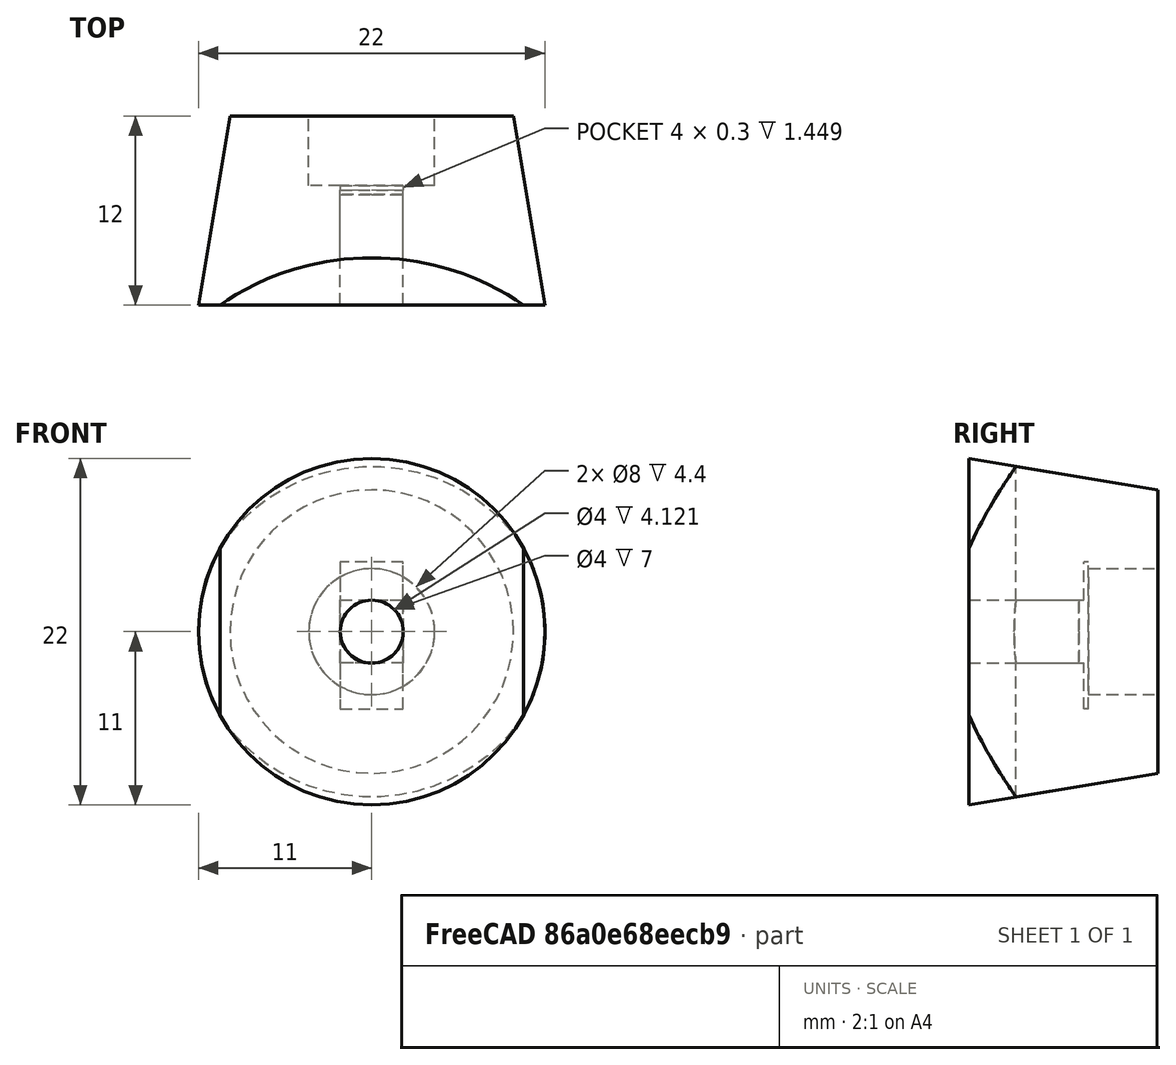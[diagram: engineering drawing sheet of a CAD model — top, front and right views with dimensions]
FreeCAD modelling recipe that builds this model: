
FCSTD DOCUMENT  (FreeCAD 0.19R)
Label: TrikeBumpers
License: All rights reserved
LicenseURL: http://en.wikipedia.org/wiki/All_rights_reserved
objects: Sketcher::SketchObject×4, PartDesign::Pocket×2, PartDesign::Revolution×1, Part::Cylinder×1, PartDesign::Pad×1, PartDesign::Body×1, Part::Cut×1, Mesh::Feature×1
note: 15 computed .brp shape members not serialized (recipe doc carries the construction recipe); baked Part::Feature solids carry a one-line shape summary decoded from their .brp

FEATURE [Sketcher::SketchObject] Sketch
  FullyConstrained = true
  MapMode = 5
  Support = -> [XY_Plane]
  sketch-geometry (6):
    g0: LineSegment StartX=2 StartY=7 StartZ=0 EndX=4 EndY=7 EndZ=0
    g1: LineSegment StartX=4 StartY=7 StartZ=0 EndX=4 EndY=12 EndZ=0
    g2: LineSegment StartX=4 StartY=12 StartZ=0 EndX=9 EndY=12 EndZ=0
    g3: LineSegment StartX=9 StartY=12 StartZ=0 EndX=11 EndY=0 EndZ=0
    g4: LineSegment StartX=11 StartY=0 StartZ=0 EndX=2 EndY=0 EndZ=0
    g5: LineSegment StartX=2 StartY=0 StartZ=0 EndX=2 EndY=7 EndZ=0
  constraints (18):
    c: Horizontal(g0)
    c: Coincident(g0,g1)
    c: Vertical(g1)
    c: Coincident(g1,g2)
    c: Horizontal(g2)
    c: Coincident(g2,g3)
    c: PointOnObject(g3,g-1)
    c: Coincident(g3,g4)
    c: PointOnObject(g4,g-1)
    c: Coincident(g4,g5)
    c: Coincident(g5,g0)
    c: Vertical(g5)
    c: DistanceX(g3) = 11
    c: DistanceX(g2) = 9
    c: DistanceX(g0) = 2
    c: DistanceX(g1) = 4
    c: Distance(g1) = 5
    c: DistanceY(g1) = 12
FEATURE [PartDesign::Revolution] Revolution
  Angle = 360
  Axis = (0,1,0)
  Base = (0,0,0)
  Profile = -> Sketch
  ReferenceAxis = -> Sketch [V_Axis]
  Reversed = true
FEATURE [Part::Cylinder] Cylinder
  Angle = 360
  AttacherType = Attacher::AttachEngine3D
  Height = 100
  Placement = pos=(0,-14,-20) rot=(0,0,1;0rad)
  Radius = 17
FEATURE [Sketcher::SketchObject] Sketch001
  FullyConstrained = false
  MapMode = 5
  Placement = pos=(0,7,0) rot=(0,0.707107,0.707107;3.14159rad)
  Support = -> [Revolution]
  sketch-geometry (4):
    g0: LineSegment StartX=-4.35972 StartY=4.85502 StartZ=0 EndX=4.65727 EndY=4.85502 EndZ=0
    g1: LineSegment StartX=4.65727 StartY=4.85502 StartZ=0 EndX=4.65727 EndY=-5.02854 EndZ=0
    g2: LineSegment StartX=4.65727 StartY=-5.02854 StartZ=0 EndX=-4.35972 EndY=-5.02854 EndZ=0
    g3: LineSegment StartX=-4.35972 StartY=-5.02854 StartZ=0 EndX=-4.35972 EndY=4.85502 EndZ=0
  constraints (8):
    c: Coincident(g0,g1)
    c: Coincident(g1,g2)
    c: Coincident(g2,g3)
    c: Coincident(g3,g0)
    c: Horizontal(g0)
    c: Horizontal(g2)
    c: Vertical(g1)
    c: Vertical(g3)
FEATURE [PartDesign::Pad] Pad
  BaseFeature = -> Revolution
  Direction = (1,1,1)
  Length = 0.6
  Length2 = 100
  Profile = -> Sketch001
  Type = 0
FEATURE [Sketcher::SketchObject] Sketch002
  FullyConstrained = false
  MapMode = 5
  Placement = pos=(0,7.6,-1.4e-15) rot=(0,0.707107,0.707107;3.14159rad)
  Support = -> [Pad]
  sketch-geometry (4):
    g0: LineSegment StartX=-2 StartY=4.41259 StartZ=0 EndX=2 EndY=4.41259 EndZ=0
    g1: LineSegment StartX=2 StartY=4.41259 StartZ=0 EndX=2 EndY=-4.91303 EndZ=0
    g2: LineSegment StartX=2 StartY=-4.91303 StartZ=0 EndX=-2 EndY=-4.91303 EndZ=0
    g3: LineSegment StartX=-2 StartY=-4.91303 StartZ=0 EndX=-2 EndY=4.41259 EndZ=0
  constraints (9):
    c: Coincident(g0,g1)
    c: Coincident(g1,g2)
    c: Coincident(g2,g3)
    c: Coincident(g3,g0)
    c: Horizontal(g2)
    c: Vertical(g1)
    c: Vertical(g3)
    c: Distance(g0) = 4
    c: Symmetric(g0,g0,g-2)
FEATURE [PartDesign::Pocket] Pocket
  BaseFeature = -> Pad
  Length = 0.3
  Length2 = 100
  Profile = -> Sketch002
  Type = 0
FEATURE [Sketcher::SketchObject] Sketch003
  FullyConstrained = true
  MapMode = 5
  Placement = pos=(0,7,-1.3e-15) rot=(1,0,0;1.5708rad)
  Support = -> [Pocket]
  sketch-geometry (4):
    g0: LineSegment StartX=-2 StartY=2 StartZ=0 EndX=2 EndY=2 EndZ=0
    g1: LineSegment StartX=2 StartY=2 StartZ=0 EndX=2 EndY=-2 EndZ=0
    g2: LineSegment StartX=2 StartY=-2 StartZ=0 EndX=-2 EndY=-2 EndZ=0
    g3: LineSegment StartX=-2 StartY=-2 StartZ=0 EndX=-2 EndY=2 EndZ=0
  constraints (11):
    c: Coincident(g0,g1)
    c: Coincident(g1,g2)
    c: Coincident(g2,g3)
    c: Coincident(g3,g0)
    c: Horizontal(g0)
    c: Horizontal(g2)
    c: Vertical(g1)
    c: Vertical(g3)
    c: Symmetric(g1,g0,g-1)
    c: Distance(g0) = 4
    c: Equal(g1,g2)
FEATURE [PartDesign::Pocket] Pocket001
  BaseFeature = -> Pocket
  Length = 0.3
  Length2 = 100
  Profile = -> Sketch003
  Type = 0
FEATURE [PartDesign::Body] Body
  Group = -> [Sketch,Revolution,Sketch001,Pad,Sketch002,Pocket,Sketch003,Pocket001]
  Origin = -> Origin
  Tip = -> Pocket001
FEATURE [Part::Cut] Cut
  Base = -> Pocket001
  Tool = -> Cylinder
FEATURE [Mesh::Feature] Mesh  label="Cut (Meshed)"
